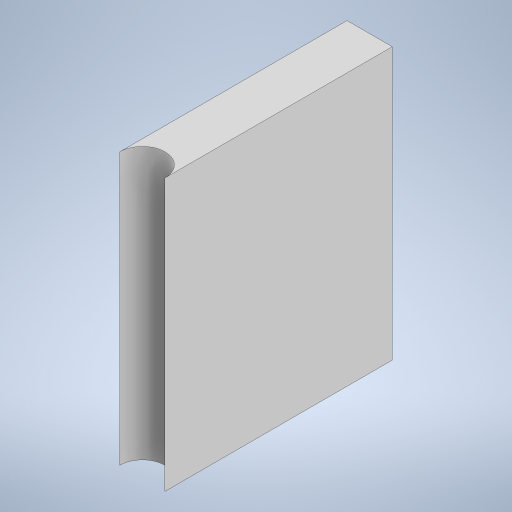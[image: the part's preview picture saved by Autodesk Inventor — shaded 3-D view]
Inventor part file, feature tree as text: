
AUTODESK INVENTOR PART (.ipt)
format: ipt  version: 2024.2 (Build 282272000, 272)  size: 194,560 bytes
history: native  units: in
note: dims shown in document units (in); Inventor stores cm internally (conversion verified against a paired STEP export)
features: extrude x1, sketch x1
ambient origin geometry x8: Origin, YZ Plane, XZ Plane, XY Plane, X Axis, Y Axis, Z Axis, Center Point
bodies: Solid1 (feature_tree)
feature tree (2):
  extrude  "Extrusion1"  Depth=0.5in
  sketch  "Sketch1"  dims[d0=0.25in d1=0.5in d2=3.0in d3=0.0in]
